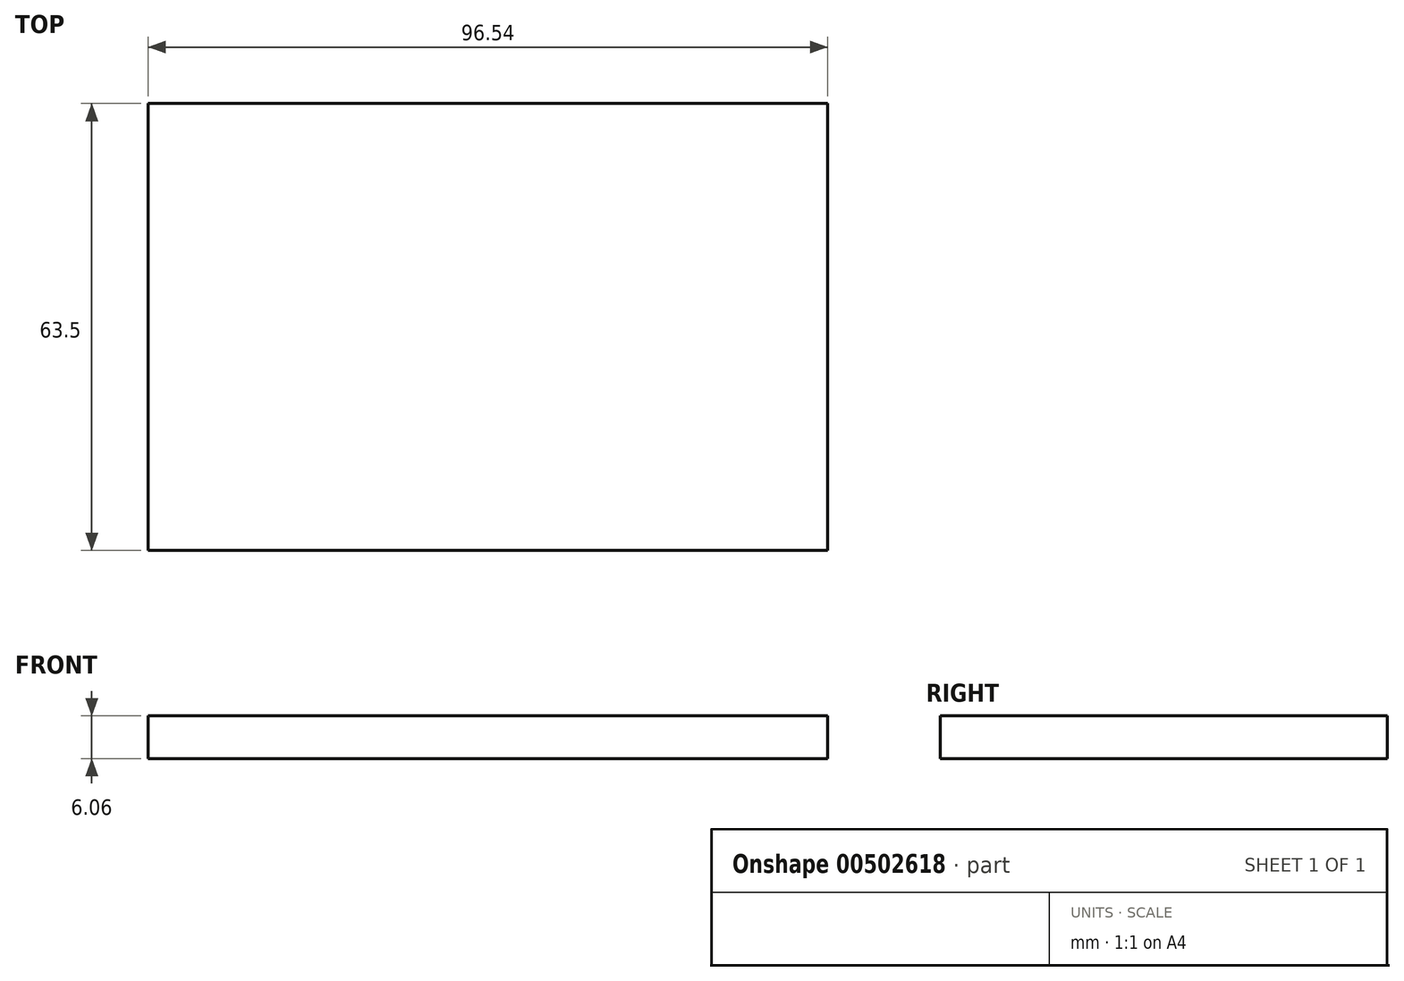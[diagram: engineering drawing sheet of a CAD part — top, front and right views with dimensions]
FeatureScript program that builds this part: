
annotation { "Feature Type Name" : "Feature", "Feature Type Description" : "" }
export const myFeature = defineFeature(function(context is Context, id is Id, definition is map)
    precondition{}
    {
        {
            var Q0;
            Q0=qCreatedBy(makeId("Front.planeOp"),FACE);
            var sketch = newSketch(context, id + "F0", { "sketchPlane" : qUnion([Q0])});
            skLineSegment(sketch, "E0.bottom", {"start": v(48.27, -3.03) * mm, "end": v(-48.27, -3.03) * mm});
            skLineSegment(sketch, "E0.top", {"start": v(48.27, 3.03) * mm, "end": v(-48.27, 3.03) * mm});
            skLineSegment(sketch, "E0.left", {"start": v(48.27, -3.03) * mm, "end": v(48.27, 3.03) * mm});
            skLineSegment(sketch, "E0.right", {"start": v(-48.27, -3.03) * mm, "end": v(-48.27, 3.03) * mm});
            skPoint(sketch, "E0.middle", {"position": v(0, 0) * mm});
            skSolve(sketch);
        }
        {
            var Q0;
            Q0 = qSketchRegion(id + "F0", true);
            extrude(context, id + "F1", {"entities" : qUnion([Q0]), "depth" : 31.75 * mm, "hasSecondDirection" : true, "secondDirectionOppositeDirection" : true, "secondDirectionDepth" : 31.75 * mm});
        }
    });
